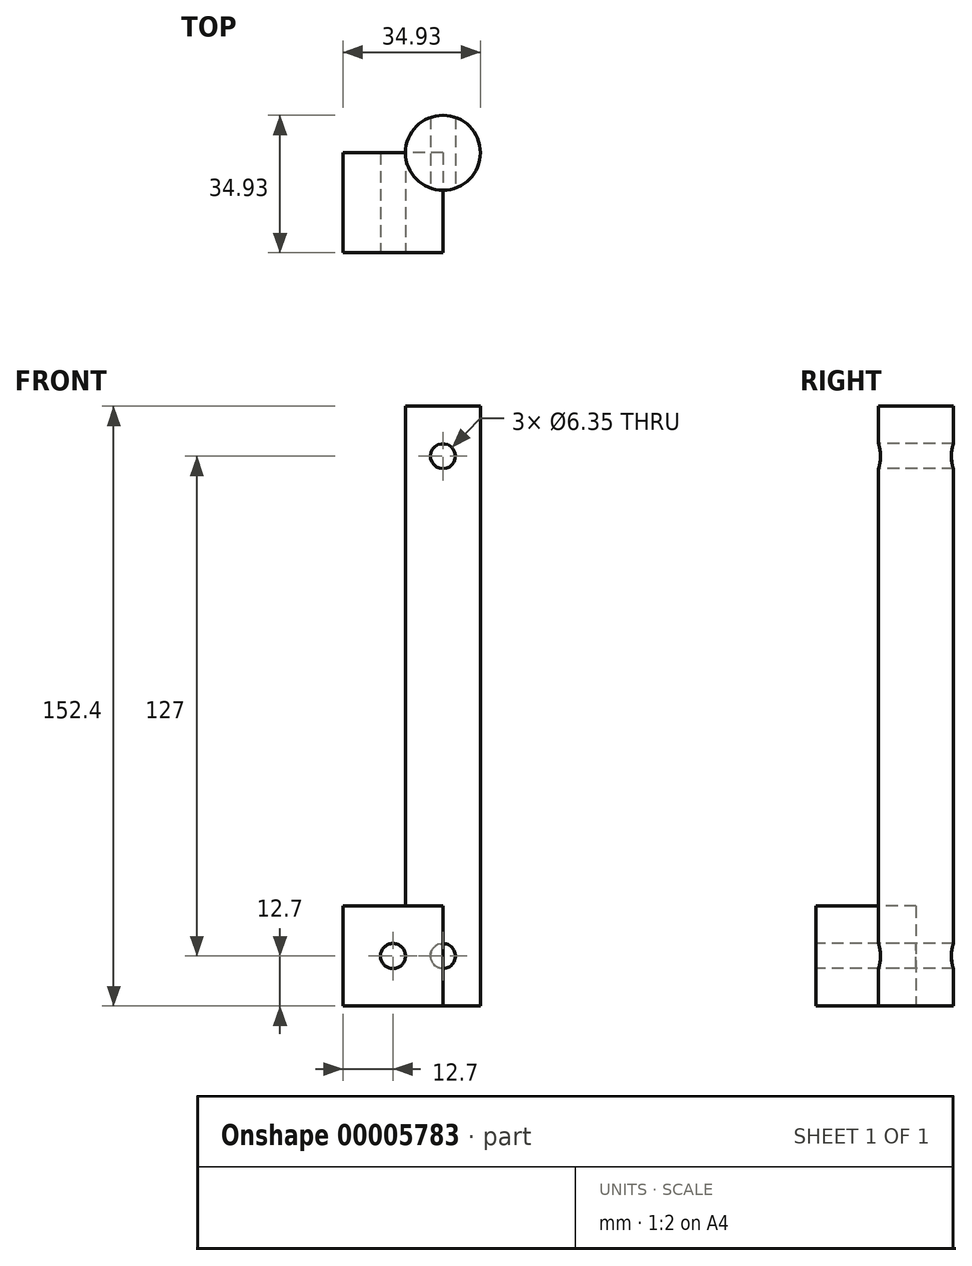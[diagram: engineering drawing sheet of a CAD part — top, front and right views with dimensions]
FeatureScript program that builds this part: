
annotation { "Feature Type Name" : "Feature", "Feature Type Description" : "" }
export const myFeature = defineFeature(function(context is Context, id is Id, definition is map)
    precondition{}
    {
        {
            var Q0;
            Q0=qCreatedBy(makeId("Top.planeOp"),FACE);
            var sketch = newSketch(context, id + "F0", { "sketchPlane" : qUnion([Q0])});
            skCircle(sketch, "E0", {"center": v(0, 0) * mm, "radius": 9.53 * mm});
            skSolve(sketch);
        }
        {
            var Q0;
            Q0=makeQuery(id+"F0.imprint","IMPRINT",FACE,{"disambiguationData":[TD([[makeQuery(id+"F0.imprint","IMPRINT",EDGE,{"derivedFrom":sQuery(id+"F0.wireOp",EDGE,"E0")}),1.0]])]});
            extrude(context, id + "F1", {"entities" : qUnion([Q0]), "depth" : 152.4 * mm});
        }
        {
            var Q0;
            Q0=qCreatedBy(makeId("Front.planeOp"),FACE);
            var sketch = newSketch(context, id + "F2", { "sketchPlane" : qUnion([Q0])});
            skLineSegment(sketch, "E1.0", {"start": v(-9.53, 0) * mm, "end": v(9.53, 0) * mm, "construction": true});
            skLineSegment(sketch, "E2.0", {"start": v(-9.53, 152.4) * mm, "end": v(9.53, 152.4) * mm, "construction": true});
            skCircle(sketch, "E3", {"center": v(0, 139.7) * mm, "radius": 3.18 * mm});
            skPoint(sketch, "E4", {"position": v(0, 152.4) * mm});
            skPoint(sketch, "E5", {"position": v(0, 0) * mm});
            skCircle(sketch, "E6", {"center": v(0, 12.7) * mm, "radius": 3.18 * mm});
            skSolve(sketch);
        }
        {
            var Q0;
            Q0 = qSketchRegion(id + "F2", true);
            extrude(context, id + "F3", {"entities" : qUnion([Q0]), "operationType" : NewBodyOperationType.REMOVE, "endBound" : BoundingType.SYMMETRIC, "oppositeDirection" : true, "depth" : 25.4 * mm});
        }
        {
            var Q0;
            Q0=qCreatedBy(makeId("Top.planeOp"),FACE);
            var sketch = newSketch(context, id + "F4", { "sketchPlane" : qUnion([Q0])});
            skLineSegment(sketch, "E7.bottom", {"start": v(0, 0) * mm, "end": v(-25.4, 0) * mm});
            skLineSegment(sketch, "E7.top", {"start": v(0, -25.4) * mm, "end": v(-25.4, -25.4) * mm});
            skLineSegment(sketch, "E7.left", {"start": v(0, 0) * mm, "end": v(0, -25.4) * mm});
            skLineSegment(sketch, "E7.right", {"start": v(-25.4, 0) * mm, "end": v(-25.4, -25.4) * mm});
            skSolve(sketch);
        }
        {
            var Q0;
            Q0=makeQuery(id+"F4.imprint","IMPRINT",FACE,{"disambiguationData":[TD([[makeQuery(id+"F4.imprint","IMPRINT",EDGE,{"derivedFrom":sQuery(id+"F4.wireOp",EDGE,"E7.bottom")}),1.0]])]});
            extrude(context, id + "F5", {"entities" : qUnion([Q0]), "depth" : 25.4 * mm});
        }
        {
            var Q0;
            Q0=makeQuery(id+"F5.opExtrude","SWEPT_FACE",FACE,{"disambiguationData":[OSD([sQuery(id+"F4.wireOp",EDGE,"E7.top")])]});
            var sketch = newSketch(context, id + "F6", { "sketchPlane" : qUnion([Q0])});
            skCircle(sketch, "E8", {"center": v(-12.7, 12.7) * mm, "radius": 3.18 * mm});
            skSolve(sketch);
        }
        {
            var Q0;
            Q0=makeQuery(id+"F6.imprint","IMPRINT",FACE,{"disambiguationData":[TD([[makeQuery(id+"F6.imprint","IMPRINT",EDGE,{"derivedFrom":sQuery(id+"F6.wireOp",EDGE,"E8")}),1.0]])]});
            var Q1;
            Q1=sQuery(id+"F6.wireOp",EDGE,"E8");
            extrude(context, id + "F7", {"entities" : qUnion([Q0]), "operationType" : NewBodyOperationType.REMOVE, "surfaceEntities" : qUnion([Q1]), "oppositeDirection" : true, "depth" : 25.4 * mm});
        }
    });
